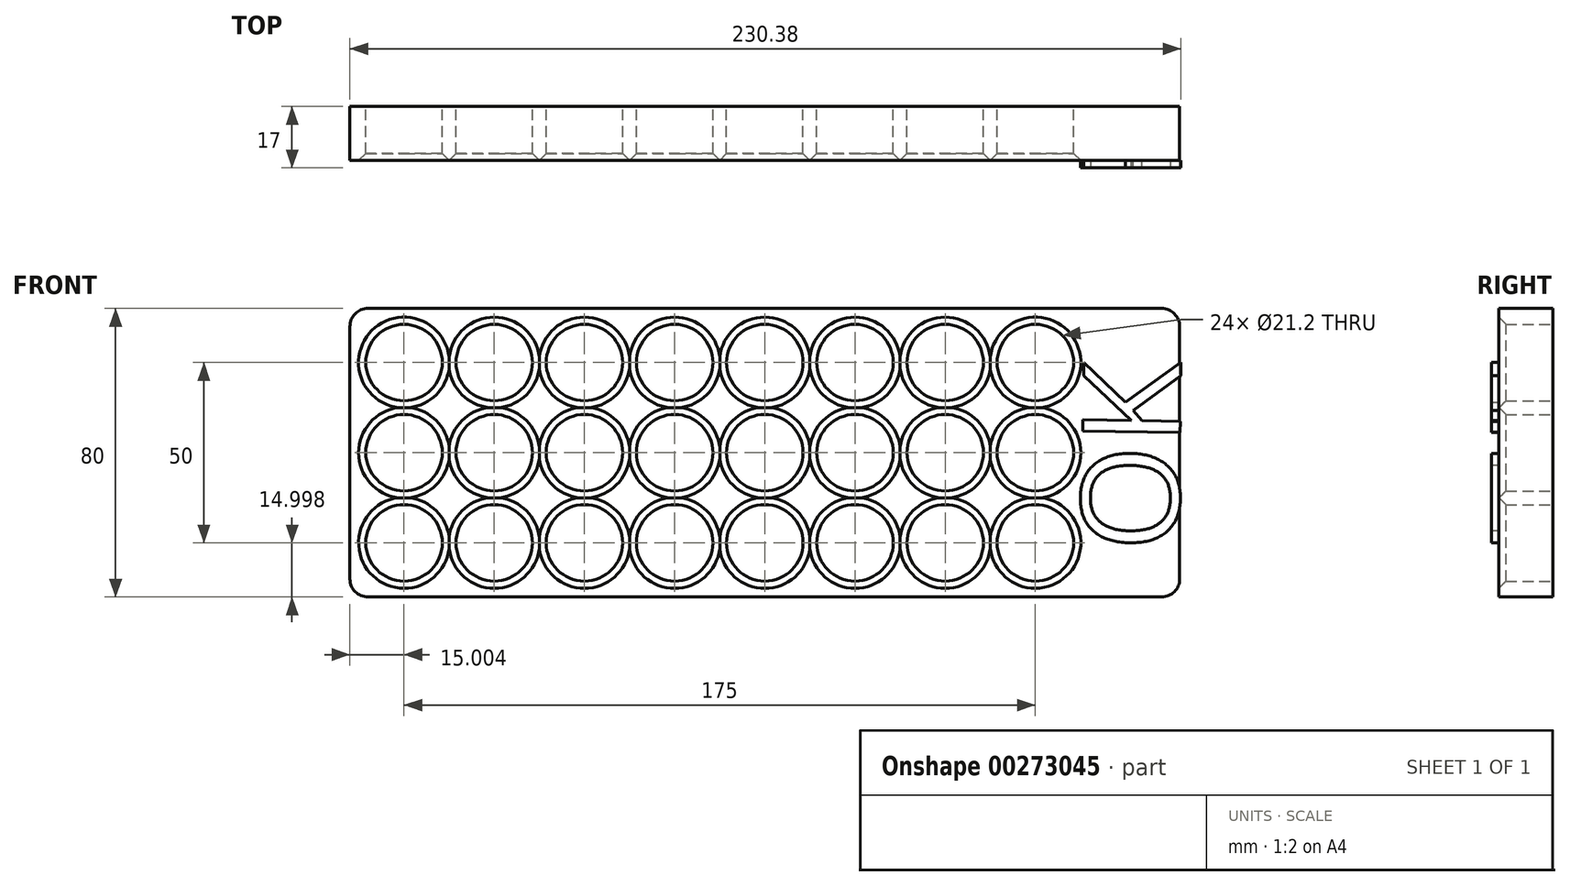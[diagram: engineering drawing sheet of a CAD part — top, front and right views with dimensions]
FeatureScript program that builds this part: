
annotation { "Feature Type Name" : "Feature", "Feature Type Description" : "" }
export const myFeature = defineFeature(function(context is Context, id is Id, definition is map)
    precondition{}
    {
        {
            var Q0;
            Q0=qCreatedBy(makeId("Front.planeOp"),FACE);
            var sketch = newSketch(context, id + "F0", { "sketchPlane" : qUnion([Q0])});
            skLineSegment(sketch, "E0.bottom", {"start": v(-104.74, 155.68) * mm, "end": v(125.26, 155.68) * mm});
            skLineSegment(sketch, "E0.top", {"start": v(-104.74, 75.68) * mm, "end": v(125.26, 75.68) * mm});
            skLineSegment(sketch, "E0.left", {"start": v(-104.74, 155.68) * mm, "end": v(-104.74, 75.68) * mm});
            skLineSegment(sketch, "E0.right", {"start": v(125.26, 155.68) * mm, "end": v(125.26, 75.68) * mm});
            skCircle(sketch, "E1", {"center": v(-89.74, 140.68) * mm, "radius": 10.6 * mm});
            skCircle(sketch, "E2.0.1.0", {"center": v(-89.74, 115.68) * mm, "radius": 10.6 * mm});
            skCircle(sketch, "E2.0.2.0", {"center": v(-89.74, 90.68) * mm, "radius": 10.6 * mm});
            skCircle(sketch, "E2.1.0.0", {"center": v(-64.74, 140.68) * mm, "radius": 10.6 * mm});
            skCircle(sketch, "E2.1.1.0", {"center": v(-64.74, 115.68) * mm, "radius": 10.6 * mm});
            skCircle(sketch, "E2.1.2.0", {"center": v(-64.74, 90.68) * mm, "radius": 10.6 * mm});
            skCircle(sketch, "E2.2.0.0", {"center": v(-39.74, 140.68) * mm, "radius": 10.6 * mm});
            skCircle(sketch, "E2.2.1.0", {"center": v(-39.74, 115.68) * mm, "radius": 10.6 * mm});
            skCircle(sketch, "E2.2.2.0", {"center": v(-39.74, 90.68) * mm, "radius": 10.6 * mm});
            skCircle(sketch, "E2.3.0.0", {"center": v(-14.74, 140.68) * mm, "radius": 10.6 * mm});
            skCircle(sketch, "E2.3.1.0", {"center": v(-14.74, 115.68) * mm, "radius": 10.6 * mm});
            skCircle(sketch, "E2.3.2.0", {"center": v(-14.74, 90.68) * mm, "radius": 10.6 * mm});
            skCircle(sketch, "E2.4.0.0", {"center": v(10.26, 140.68) * mm, "radius": 10.6 * mm});
            skCircle(sketch, "E2.4.1.0", {"center": v(10.26, 115.68) * mm, "radius": 10.6 * mm});
            skCircle(sketch, "E2.4.2.0", {"center": v(10.26, 90.68) * mm, "radius": 10.6 * mm});
            skCircle(sketch, "E2.5.0.0", {"center": v(35.26, 140.68) * mm, "radius": 10.6 * mm});
            skCircle(sketch, "E2.5.1.0", {"center": v(35.26, 115.68) * mm, "radius": 10.6 * mm});
            skCircle(sketch, "E2.5.2.0", {"center": v(35.26, 90.68) * mm, "radius": 10.6 * mm});
            skCircle(sketch, "E2.6.0.0", {"center": v(60.26, 140.68) * mm, "radius": 10.6 * mm});
            skCircle(sketch, "E2.6.1.0", {"center": v(60.26, 115.68) * mm, "radius": 10.6 * mm});
            skCircle(sketch, "E2.6.2.0", {"center": v(60.26, 90.68) * mm, "radius": 10.6 * mm});
            skCircle(sketch, "E2.7.0.0", {"center": v(85.26, 140.68) * mm, "radius": 10.6 * mm});
            skCircle(sketch, "E2.7.1.0", {"center": v(85.26, 115.68) * mm, "radius": 10.6 * mm});
            skCircle(sketch, "E2.7.2.0", {"center": v(85.26, 90.68) * mm, "radius": 10.6 * mm});
            skLineSegment(sketch, "E2.direction1", {"start": v(-89.74, 140.68) * mm, "end": v(-64.74, 140.68) * mm, "construction": true});
            skLineSegment(sketch, "E2.direction2", {"start": v(-89.74, 140.68) * mm, "end": v(-89.74, 115.68) * mm, "construction": true});
            skSolve(sketch);
        }
        {
            var Q0;
            Q0 = qSketchRegion(id + "F0", true);
            extrude(context, id + "F1", {"entities" : qUnion([Q0]), "depth" : 15 * mm});
        }
        {
            var Q0;
            Q0=makeQuery(id+"FWD52A0zWoIziQt_1.boolean.opBoolean","MERGE",EDGE,{"derivedFrom":[makeQuery(id+"F1.opExtrude","SWEPT_EDGE",EDGE,{"disambiguationData":[OSD([sQuery(id+"F0.wireOp",EDGE,"E0.bottom"),sQuery(id+"F0.wireOp",EDGE,"E0.right")])]}),makeQuery(id+"FWD52A0zWoIziQt_1.opExtrude","SWEPT_EDGE",EDGE,{"disambiguationData":[OSD([sQuery(id+"FsMENEcZQ2nr4Gj_1.wireOp",EDGE,"yo0ZsG5o-0MR3-nl2M-1CvW-6fkTD8x1XfXn.bottom"),sQuery(id+"FsMENEcZQ2nr4Gj_1.wireOp",EDGE,"yo0ZsG5o-0MR3-nl2M-1CvW-6fkTD8x1XfXn.left")])]})]});
            var Q1;
            Q1=makeQuery(id+"FWD52A0zWoIziQt_1.boolean.opBoolean","MERGE",EDGE,{"derivedFrom":[makeQuery(id+"F1.opExtrude","SWEPT_EDGE",EDGE,{"disambiguationData":[OSD([sQuery(id+"F0.wireOp",EDGE,"E0.top"),sQuery(id+"F0.wireOp",EDGE,"E0.right")])]}),makeQuery(id+"FWD52A0zWoIziQt_1.opExtrude","SWEPT_EDGE",EDGE,{"disambiguationData":[OSD([sQuery(id+"FsMENEcZQ2nr4Gj_1.wireOp",EDGE,"yo0ZsG5o-0MR3-nl2M-1CvW-6fkTD8x1XfXn.top"),sQuery(id+"FsMENEcZQ2nr4Gj_1.wireOp",EDGE,"yo0ZsG5o-0MR3-nl2M-1CvW-6fkTD8x1XfXn.left")])]})]});
            var Q2;
            Q2=makeQuery(id+"FWD52A0zWoIziQt_1.boolean.opBoolean","MERGE",EDGE,{"derivedFrom":[makeQuery(id+"F1.opExtrude","SWEPT_EDGE",EDGE,{"disambiguationData":[OSD([sQuery(id+"F0.wireOp",EDGE,"E0.bottom"),sQuery(id+"F0.wireOp",EDGE,"E0.left")])]}),makeQuery(id+"FWD52A0zWoIziQt_1.opExtrude","SWEPT_EDGE",EDGE,{"disambiguationData":[OSD([sQuery(id+"FsMENEcZQ2nr4Gj_1.wireOp",EDGE,"yo0ZsG5o-0MR3-nl2M-1CvW-6fkTD8x1XfXn.bottom"),sQuery(id+"FsMENEcZQ2nr4Gj_1.wireOp",EDGE,"yo0ZsG5o-0MR3-nl2M-1CvW-6fkTD8x1XfXn.right")])]})]});
            var Q3;
            Q3=makeQuery(id+"FWD52A0zWoIziQt_1.boolean.opBoolean","MERGE",EDGE,{"derivedFrom":[makeQuery(id+"F1.opExtrude","SWEPT_EDGE",EDGE,{"disambiguationData":[OSD([sQuery(id+"F0.wireOp",EDGE,"E0.top"),sQuery(id+"F0.wireOp",EDGE,"E0.left")])]}),makeQuery(id+"FWD52A0zWoIziQt_1.opExtrude","SWEPT_EDGE",EDGE,{"disambiguationData":[OSD([sQuery(id+"FsMENEcZQ2nr4Gj_1.wireOp",EDGE,"yo0ZsG5o-0MR3-nl2M-1CvW-6fkTD8x1XfXn.top"),sQuery(id+"FsMENEcZQ2nr4Gj_1.wireOp",EDGE,"yo0ZsG5o-0MR3-nl2M-1CvW-6fkTD8x1XfXn.right")])]})]});
            fillet(context, id + "F2", {"entities" : qUnion([Q0, Q1, Q2, Q3]), "radius" : 5 * mm, "tangentPropagation" : true, "allowEdgeOverflow" : false});
        }
        {
            var Q0;
            Q0=makeQuery(id+"F1.opExtrude","CAP_EDGE",EDGE,{"disambiguationData":[OSD([sQuery(id+"F0.wireOp",EDGE,"E2.0.5.0")])],"isStart":false});
            var Q1;
            Q1=makeQuery(id+"F1.opExtrude","CAP_EDGE",EDGE,{"disambiguationData":[OSD([sQuery(id+"F0.wireOp",EDGE,"E2.0.6.0")])],"isStart":false});
            var Q2;
            Q2=makeQuery(id+"F1.opExtrude","CAP_EDGE",EDGE,{"disambiguationData":[OSD([sQuery(id+"F0.wireOp",EDGE,"E2.0.7.0")])],"isStart":false});
            var Q3;
            Q3=makeQuery(id+"F1.opExtrude","CAP_EDGE",EDGE,{"disambiguationData":[OSD([sQuery(id+"F0.wireOp",EDGE,"E2.1.7.0")])],"isStart":false});
            var Q4;
            Q4=makeQuery(id+"F1.opExtrude","CAP_EDGE",EDGE,{"disambiguationData":[OSD([sQuery(id+"F0.wireOp",EDGE,"E2.1.6.0")])],"isStart":false});
            var Q5;
            Q5=makeQuery(id+"F1.opExtrude","CAP_EDGE",EDGE,{"disambiguationData":[OSD([sQuery(id+"F0.wireOp",EDGE,"E2.1.5.0")])],"isStart":false});
            var Q6;
            Q6=makeQuery(id+"F1.opExtrude","CAP_EDGE",EDGE,{"disambiguationData":[OSD([sQuery(id+"F0.wireOp",EDGE,"E2.0.4.0")])],"isStart":false});
            var Q7;
            Q7=makeQuery(id+"F1.opExtrude","CAP_EDGE",EDGE,{"disambiguationData":[OSD([sQuery(id+"F0.wireOp",EDGE,"E2.0.3.0")])],"isStart":false});
            var Q8;
            Q8=makeQuery(id+"F1.opExtrude","CAP_EDGE",EDGE,{"disambiguationData":[OSD([sQuery(id+"F0.wireOp",EDGE,"E2.0.2.0")])],"isStart":false});
            var Q9;
            Q9=makeQuery(id+"F1.opExtrude","CAP_EDGE",EDGE,{"disambiguationData":[OSD([sQuery(id+"F0.wireOp",EDGE,"E2.0.1.0")])],"isStart":false});
            var Q10;
            Q10=makeQuery(id+"F1.opExtrude","CAP_EDGE",EDGE,{"disambiguationData":[OSD([sQuery(id+"F0.wireOp",EDGE,"E1")])],"isStart":false});
            var Q11;
            Q11=makeQuery(id+"F1.opExtrude","CAP_EDGE",EDGE,{"disambiguationData":[OSD([sQuery(id+"F0.wireOp",EDGE,"E2.1.0.0")])],"isStart":false});
            var Q12;
            Q12=makeQuery(id+"F1.opExtrude","CAP_EDGE",EDGE,{"disambiguationData":[OSD([sQuery(id+"F0.wireOp",EDGE,"E2.1.1.0")])],"isStart":false});
            var Q13;
            Q13=makeQuery(id+"F1.opExtrude","CAP_EDGE",EDGE,{"disambiguationData":[OSD([sQuery(id+"F0.wireOp",EDGE,"E2.1.2.0")])],"isStart":false});
            var Q14;
            Q14=makeQuery(id+"F1.opExtrude","CAP_EDGE",EDGE,{"disambiguationData":[OSD([sQuery(id+"F0.wireOp",EDGE,"E2.1.3.0")])],"isStart":false});
            var Q15;
            Q15=makeQuery(id+"F1.opExtrude","CAP_EDGE",EDGE,{"disambiguationData":[OSD([sQuery(id+"F0.wireOp",EDGE,"E2.1.4.0")])],"isStart":false});
            var Q16;
            Q16=makeQuery(id+"F1.opExtrude","CAP_EDGE",EDGE,{"disambiguationData":[OSD([sQuery(id+"F0.wireOp",EDGE,"E2.2.7.0")])],"isStart":false});
            var Q17;
            Q17=makeQuery(id+"F1.opExtrude","CAP_EDGE",EDGE,{"disambiguationData":[OSD([sQuery(id+"F0.wireOp",EDGE,"E2.2.6.0")])],"isStart":false});
            var Q18;
            Q18=makeQuery(id+"F1.opExtrude","CAP_EDGE",EDGE,{"disambiguationData":[OSD([sQuery(id+"F0.wireOp",EDGE,"E2.2.5.0")])],"isStart":false});
            var Q19;
            Q19=makeQuery(id+"F1.opExtrude","CAP_EDGE",EDGE,{"disambiguationData":[OSD([sQuery(id+"F0.wireOp",EDGE,"E2.2.4.0")])],"isStart":false});
            var Q20;
            Q20=makeQuery(id+"F1.opExtrude","CAP_EDGE",EDGE,{"disambiguationData":[OSD([sQuery(id+"F0.wireOp",EDGE,"E2.2.3.0")])],"isStart":false});
            var Q21;
            Q21=makeQuery(id+"F1.opExtrude","CAP_EDGE",EDGE,{"disambiguationData":[OSD([sQuery(id+"F0.wireOp",EDGE,"E2.2.2.0")])],"isStart":false});
            var Q22;
            Q22=makeQuery(id+"F1.opExtrude","CAP_EDGE",EDGE,{"disambiguationData":[OSD([sQuery(id+"F0.wireOp",EDGE,"E2.2.1.0")])],"isStart":false});
            var Q23;
            Q23=makeQuery(id+"F1.opExtrude","CAP_EDGE",EDGE,{"disambiguationData":[OSD([sQuery(id+"F0.wireOp",EDGE,"E2.2.0.0")])],"isStart":false});
            var Q24;
            Q24=makeQuery(id+"F1.opExtrude","CAP_EDGE",EDGE,{"disambiguationData":[OSD([sQuery(id+"F0.wireOp",EDGE,"E2.3.0.0")])],"isStart":false});
            var Q25;
            Q25=makeQuery(id+"F1.opExtrude","CAP_EDGE",EDGE,{"disambiguationData":[OSD([sQuery(id+"F0.wireOp",EDGE,"E2.3.1.0")])],"isStart":false});
            var Q26;
            Q26=makeQuery(id+"F1.opExtrude","CAP_EDGE",EDGE,{"disambiguationData":[OSD([sQuery(id+"F0.wireOp",EDGE,"E2.3.2.0")])],"isStart":false});
            var Q27;
            Q27=makeQuery(id+"F1.opExtrude","CAP_EDGE",EDGE,{"disambiguationData":[OSD([sQuery(id+"F0.wireOp",EDGE,"E2.3.3.0")])],"isStart":false});
            var Q28;
            Q28=makeQuery(id+"F1.opExtrude","CAP_EDGE",EDGE,{"disambiguationData":[OSD([sQuery(id+"F0.wireOp",EDGE,"E2.3.4.0")])],"isStart":false});
            var Q29;
            Q29=makeQuery(id+"F1.opExtrude","CAP_EDGE",EDGE,{"disambiguationData":[OSD([sQuery(id+"F0.wireOp",EDGE,"E2.3.5.0")])],"isStart":false});
            var Q30;
            Q30=makeQuery(id+"F1.opExtrude","CAP_EDGE",EDGE,{"disambiguationData":[OSD([sQuery(id+"F0.wireOp",EDGE,"E2.3.6.0")])],"isStart":false});
            var Q31;
            Q31=makeQuery(id+"F1.opExtrude","CAP_EDGE",EDGE,{"disambiguationData":[OSD([sQuery(id+"F0.wireOp",EDGE,"E2.3.7.0")])],"isStart":false});
            var Q32;
            Q32=makeQuery(id+"F1.opExtrude","CAP_EDGE",EDGE,{"disambiguationData":[OSD([sQuery(id+"F0.wireOp",EDGE,"E2.4.7.0")])],"isStart":false});
            var Q33;
            Q33=makeQuery(id+"F1.opExtrude","CAP_EDGE",EDGE,{"disambiguationData":[OSD([sQuery(id+"F0.wireOp",EDGE,"E2.4.6.0")])],"isStart":false});
            var Q34;
            Q34=makeQuery(id+"F1.opExtrude","CAP_EDGE",EDGE,{"disambiguationData":[OSD([sQuery(id+"F0.wireOp",EDGE,"E2.4.5.0")])],"isStart":false});
            var Q35;
            Q35=makeQuery(id+"F1.opExtrude","CAP_EDGE",EDGE,{"disambiguationData":[OSD([sQuery(id+"F0.wireOp",EDGE,"E2.4.4.0")])],"isStart":false});
            var Q36;
            Q36=makeQuery(id+"F1.opExtrude","CAP_EDGE",EDGE,{"disambiguationData":[OSD([sQuery(id+"F0.wireOp",EDGE,"E2.4.3.0")])],"isStart":false});
            var Q37;
            Q37=makeQuery(id+"F1.opExtrude","CAP_EDGE",EDGE,{"disambiguationData":[OSD([sQuery(id+"F0.wireOp",EDGE,"E2.4.2.0")])],"isStart":false});
            var Q38;
            Q38=makeQuery(id+"F1.opExtrude","CAP_EDGE",EDGE,{"disambiguationData":[OSD([sQuery(id+"F0.wireOp",EDGE,"E2.4.1.0")])],"isStart":false});
            var Q39;
            Q39=makeQuery(id+"F1.opExtrude","CAP_EDGE",EDGE,{"disambiguationData":[OSD([sQuery(id+"F0.wireOp",EDGE,"E2.4.0.0")])],"isStart":false});
            var Q40;
            Q40=makeQuery(id+"F1.opExtrude","CAP_EDGE",EDGE,{"disambiguationData":[OSD([sQuery(id+"F0.wireOp",EDGE,"E2.5.0.0")])],"isStart":false});
            var Q41;
            Q41=makeQuery(id+"F1.opExtrude","CAP_EDGE",EDGE,{"disambiguationData":[OSD([sQuery(id+"F0.wireOp",EDGE,"E2.5.1.0")])],"isStart":false});
            var Q42;
            Q42=makeQuery(id+"F1.opExtrude","CAP_EDGE",EDGE,{"disambiguationData":[OSD([sQuery(id+"F0.wireOp",EDGE,"E2.6.0.0")])],"isStart":false});
            var Q43;
            Q43=makeQuery(id+"F1.opExtrude","CAP_EDGE",EDGE,{"disambiguationData":[OSD([sQuery(id+"F0.wireOp",EDGE,"E2.6.1.0")])],"isStart":false});
            var Q44;
            Q44=makeQuery(id+"F1.opExtrude","CAP_EDGE",EDGE,{"disambiguationData":[OSD([sQuery(id+"F0.wireOp",EDGE,"E2.7.0.0")])],"isStart":false});
            var Q45;
            Q45=makeQuery(id+"F1.opExtrude","CAP_EDGE",EDGE,{"disambiguationData":[OSD([sQuery(id+"F0.wireOp",EDGE,"E2.7.1.0")])],"isStart":false});
            var Q46;
            Q46=makeQuery(id+"F1.opExtrude","CAP_EDGE",EDGE,{"disambiguationData":[OSD([sQuery(id+"F0.wireOp",EDGE,"E2.5.2.0")])],"isStart":false});
            var Q47;
            Q47=makeQuery(id+"F1.opExtrude","CAP_EDGE",EDGE,{"disambiguationData":[OSD([sQuery(id+"F0.wireOp",EDGE,"E2.6.2.0")])],"isStart":false});
            var Q48;
            Q48=makeQuery(id+"F1.opExtrude","CAP_EDGE",EDGE,{"disambiguationData":[OSD([sQuery(id+"F0.wireOp",EDGE,"E2.5.3.0")])],"isStart":false});
            var Q49;
            Q49=makeQuery(id+"F1.opExtrude","CAP_EDGE",EDGE,{"disambiguationData":[OSD([sQuery(id+"F0.wireOp",EDGE,"E2.6.3.0")])],"isStart":false});
            var Q50;
            Q50=makeQuery(id+"F1.opExtrude","CAP_EDGE",EDGE,{"disambiguationData":[OSD([sQuery(id+"F0.wireOp",EDGE,"E2.7.2.0")])],"isStart":false});
            var Q51;
            Q51=makeQuery(id+"F1.opExtrude","CAP_EDGE",EDGE,{"disambiguationData":[OSD([sQuery(id+"F0.wireOp",EDGE,"E2.7.3.0")])],"isStart":false});
            var Q52;
            Q52=makeQuery(id+"F1.opExtrude","CAP_EDGE",EDGE,{"disambiguationData":[OSD([sQuery(id+"F0.wireOp",EDGE,"E2.5.4.0")])],"isStart":false});
            var Q53;
            Q53=makeQuery(id+"F1.opExtrude","CAP_EDGE",EDGE,{"disambiguationData":[OSD([sQuery(id+"F0.wireOp",EDGE,"E2.6.4.0")])],"isStart":false});
            var Q54;
            Q54=makeQuery(id+"F1.opExtrude","CAP_EDGE",EDGE,{"disambiguationData":[OSD([sQuery(id+"F0.wireOp",EDGE,"E2.5.5.0")])],"isStart":false});
            var Q55;
            Q55=makeQuery(id+"F1.opExtrude","CAP_EDGE",EDGE,{"disambiguationData":[OSD([sQuery(id+"F0.wireOp",EDGE,"E2.6.5.0")])],"isStart":false});
            var Q56;
            Q56=makeQuery(id+"F1.opExtrude","CAP_EDGE",EDGE,{"disambiguationData":[OSD([sQuery(id+"F0.wireOp",EDGE,"E2.7.4.0")])],"isStart":false});
            var Q57;
            Q57=makeQuery(id+"F1.opExtrude","CAP_EDGE",EDGE,{"disambiguationData":[OSD([sQuery(id+"F0.wireOp",EDGE,"E2.7.5.0")])],"isStart":false});
            var Q58;
            Q58=makeQuery(id+"F1.opExtrude","CAP_EDGE",EDGE,{"disambiguationData":[OSD([sQuery(id+"F0.wireOp",EDGE,"E2.7.6.0")])],"isStart":false});
            var Q59;
            Q59=makeQuery(id+"F1.opExtrude","CAP_EDGE",EDGE,{"disambiguationData":[OSD([sQuery(id+"F0.wireOp",EDGE,"E2.6.6.0")])],"isStart":false});
            var Q60;
            Q60=makeQuery(id+"F1.opExtrude","CAP_EDGE",EDGE,{"disambiguationData":[OSD([sQuery(id+"F0.wireOp",EDGE,"E2.5.6.0")])],"isStart":false});
            var Q61;
            Q61=makeQuery(id+"F1.opExtrude","CAP_EDGE",EDGE,{"disambiguationData":[OSD([sQuery(id+"F0.wireOp",EDGE,"E2.5.7.0")])],"isStart":false});
            var Q62;
            Q62=makeQuery(id+"F1.opExtrude","CAP_EDGE",EDGE,{"disambiguationData":[OSD([sQuery(id+"F0.wireOp",EDGE,"E2.6.7.0")])],"isStart":false});
            var Q63;
            Q63=makeQuery(id+"F1.opExtrude","CAP_EDGE",EDGE,{"disambiguationData":[OSD([sQuery(id+"F0.wireOp",EDGE,"E2.7.7.0")])],"isStart":false});
            chamfer(context, id + "F3", {"entities" : qUnion([Q0, Q1, Q2, Q3, Q4, Q5, Q6, Q7, Q8, Q9, Q10, Q11, Q12, Q13, Q14, Q15, Q16, Q17, Q18, Q19, Q20, Q21, Q22, Q23, Q24, Q25, Q26, Q27, Q28, Q29, Q30, Q31, Q32, Q33, Q34, Q35, Q36, Q37, Q38, Q39, Q40, Q41, Q42, Q43, Q44, Q45, Q46, Q47, Q48, Q49, Q50, Q51, Q52, Q53, Q54, Q55, Q56, Q57, Q58, Q59, Q60, Q61, Q62, Q63]), "width" : 2 * mm, "tangentPropagation" : true});
        }
        {
            var Q0;
            Q0=makeQuery(id+"F3.opChamfer","SPLIT",FACE,{"disambiguationData":[OD(14.0)],"derivedFrom":makeQuery(id+"F1.opExtrude","CAP_FACE",FACE,{"disambiguationData":[OSD([sQuery(id+"F0.wireOp",EDGE,"E0.bottom"),sQuery(id+"F0.wireOp",EDGE,"E0.top"),sQuery(id+"F0.wireOp",EDGE,"E0.left"),sQuery(id+"F0.wireOp",EDGE,"E0.right"),sQuery(id+"F0.wireOp",EDGE,"E1"),sQuery(id+"F0.wireOp",EDGE,"E2.0.1.0"),sQuery(id+"F0.wireOp",EDGE,"E2.0.2.0"),sQuery(id+"F0.wireOp",EDGE,"E2.1.0.0"),sQuery(id+"F0.wireOp",EDGE,"E2.1.1.0"),sQuery(id+"F0.wireOp",EDGE,"E2.1.2.0"),sQuery(id+"F0.wireOp",EDGE,"E2.2.0.0"),sQuery(id+"F0.wireOp",EDGE,"E2.2.1.0"),sQuery(id+"F0.wireOp",EDGE,"E2.2.2.0"),sQuery(id+"F0.wireOp",EDGE,"E2.3.0.0"),sQuery(id+"F0.wireOp",EDGE,"E2.3.1.0"),sQuery(id+"F0.wireOp",EDGE,"E2.3.2.0"),sQuery(id+"F0.wireOp",EDGE,"E2.4.0.0"),sQuery(id+"F0.wireOp",EDGE,"E2.4.1.0"),sQuery(id+"F0.wireOp",EDGE,"E2.4.2.0"),sQuery(id+"F0.wireOp",EDGE,"E2.5.0.0"),sQuery(id+"F0.wireOp",EDGE,"E2.5.1.0"),sQuery(id+"F0.wireOp",EDGE,"E2.5.2.0"),sQuery(id+"F0.wireOp",EDGE,"E2.6.0.0"),sQuery(id+"F0.wireOp",EDGE,"E2.6.1.0"),sQuery(id+"F0.wireOp",EDGE,"E2.6.2.0"),sQuery(id+"F0.wireOp",EDGE,"E2.7.0.0"),sQuery(id+"F0.wireOp",EDGE,"E2.7.1.0"),sQuery(id+"F0.wireOp",EDGE,"E2.7.2.0")])],"isStart":false})});
            var sketch = newSketch(context, id + "F4", { "sketchPlane" : qUnion([Q0])});
            skText(sketch, "E3", { "text": "OK", "fontName": "OpenSans-Regular.ttf"});
            const initialGuessF4  = {"E3": [0.12485, 0.0882, 0.0151, 0.99989, 0.02716]};
            skSetInitialGuess(sketch, initialGuessF4);
            skSolve(sketch);
        }
        {
            var Q0;
            Q0 = qSketchRegion(id + "F4", true);
            extrude(context, id + "F5", {"entities" : qUnion([Q0]), "operationType" : NewBodyOperationType.ADD, "depth" : 2 * mm});
        }
    });
